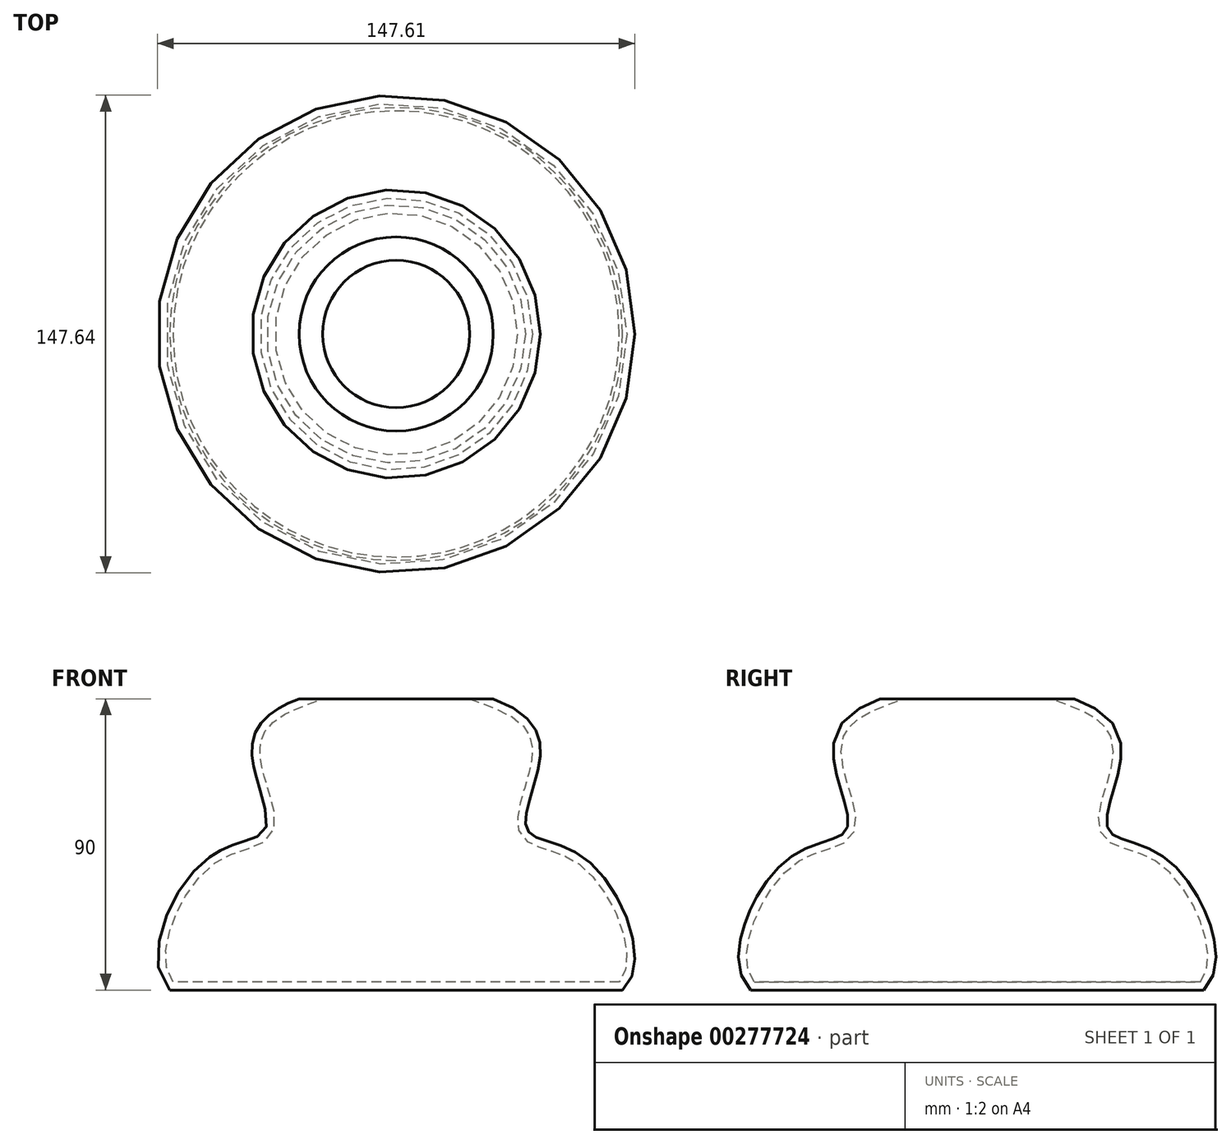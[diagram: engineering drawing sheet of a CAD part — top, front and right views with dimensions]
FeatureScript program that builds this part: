
annotation { "Feature Type Name" : "Feature", "Feature Type Description" : "" }
export const myFeature = defineFeature(function(context is Context, id is Id, definition is map)
    precondition{}
    {
        {
            var Q0;
            Q0=qCreatedBy(makeId("Front.planeOp"),FACE);
            var sketch = newSketch(context, id + "F0", { "sketchPlane" : qUnion([Q0])});
            skLineSegment(sketch, "E0", {"start": v(0, 45) * mm, "end": v(0, -45) * mm});
            skLineSegment(sketch, "E1", {"start": v(0, -45) * mm, "end": v(70, -45) * mm});
            skLineSegment(sketch, "E2", {"start": v(0, 45) * mm, "end": v(30, 45) * mm});
            skFitSpline(sketch, "E3", {"points": [v(30, 45) * mm, v(44.2, 24.77) * mm, v(40.5, 4.58) * mm, v(58.86, -4.7) * mm, v(70, -45) * mm], "startDerivative": vector(166.8, -61.33) * mm, "endDerivative": vector(-89.09, -79.26) * mm});
            skSolve(sketch);
        }
        {
            var Q0;
            Q0 = qSketchRegion(id + "F0", true);
            var Q1;
            Q1=sQuery(id+"F0.wireOp",EDGE,"E0");
            revolve(context, id + "F1", {"entities" : qUnion([Q0]), "axis" : qUnion([Q1]), "revolveType" : RevolveType.FULL});
        }
        {
            var Q0;
            Q0=makeQuery(id+"F1.opRevolve","SWEPT_FACE",FACE,{"disambiguationData":[OSD([sQuery(id+"F0.wireOp",EDGE,"E2")])]});
            shell(context, id + "F2", {"entities" : qUnion([Q0]), "thickness" : 2.5 * mm});
        }
    });
